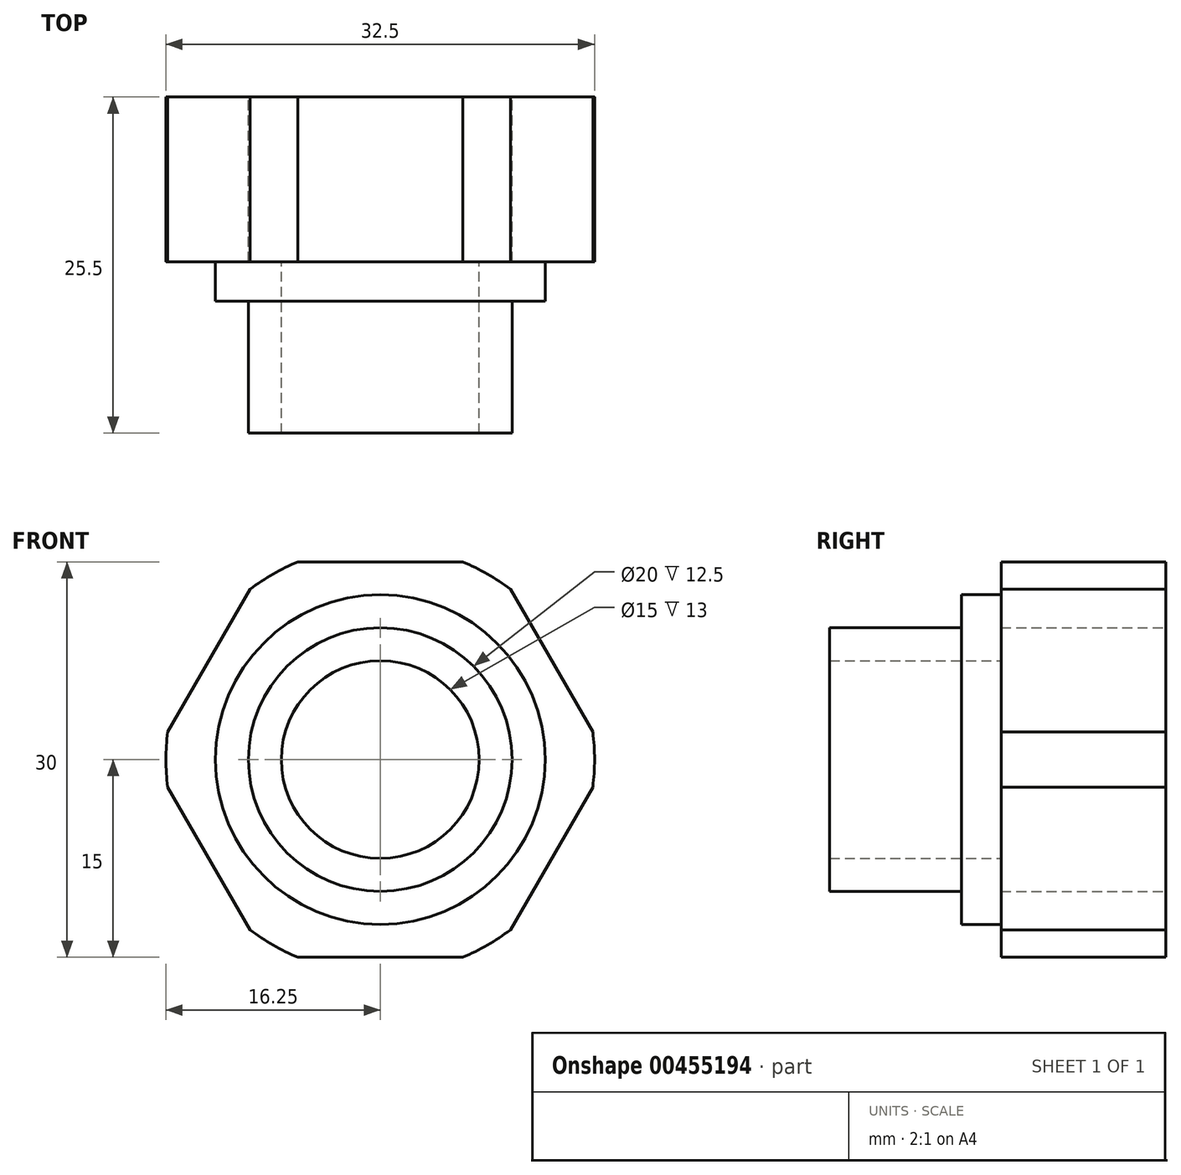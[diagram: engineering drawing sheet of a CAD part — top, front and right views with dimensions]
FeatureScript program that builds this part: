
annotation { "Feature Type Name" : "Feature", "Feature Type Description" : "" }
export const myFeature = defineFeature(function(context is Context, id is Id, definition is map)
    precondition{}
    {
        {
            var Q0;
            Q0=qCreatedBy(makeId("Front.planeOp"),FACE);
            var sketch = newSketch(context, id + "F0", { "sketchPlane" : qUnion([Q0])});
            skCircle(sketch, "E0.cCircle", {"center": v(0, 0) * mm, "radius": 15 * mm, "construction": true});
            skLineSegment(sketch, "E0.0", {"start": v(-8.66, 15) * mm, "end": v(8.66, 15) * mm});
            skLineSegment(sketch, "E0.1", {"start": v(8.66, 15) * mm, "end": v(17.32, 0) * mm});
            skLineSegment(sketch, "E0.2", {"start": v(17.32, 0) * mm, "end": v(8.66, -15) * mm});
            skLineSegment(sketch, "E0.3", {"start": v(8.66, -15) * mm, "end": v(-8.66, -15) * mm});
            skLineSegment(sketch, "E0.4", {"start": v(-8.66, -15) * mm, "end": v(-17.32, 0) * mm});
            skLineSegment(sketch, "E0.5", {"start": v(-17.32, 0) * mm, "end": v(-8.66, 15) * mm});
            skPoint(sketch, "E0.0.midPoint", {"position": v(0, 15) * mm});
            skCircle(sketch, "E1", {"center": v(0, 0) * mm, "radius": 10 * mm});
            skCircle(sketch, "E2", {"center": v(0, 0) * mm, "radius": 16.25 * mm});
            skSolve(sketch);
        }
        {
            var Q0;
            Q0=makeQuery(id+"F0.imprint","IMPRINT",FACE,{"disambiguationData":[TD([[makeQuery(id+"F0.imprint","IMPRINT",EDGE,{"derivedFrom":sQuery(id+"F0.wireOp",EDGE,"E1")}),-1.0]])]});
            extrude(context, id + "F1", {"entities" : qUnion([Q0]), "depth" : 12.5 * mm});
        }
        {
            var Q0;
            Q0=makeQuery(id+"F1.opExtrude","CAP_FACE",FACE,{"disambiguationData":[OSD([sQuery(id+"F0.wireOp",EDGE,"E0.0"),sQuery(id+"F0.wireOp",EDGE,"E0.1"),sQuery(id+"F0.wireOp",EDGE,"E0.2"),sQuery(id+"F0.wireOp",EDGE,"E0.3"),sQuery(id+"F0.wireOp",EDGE,"E0.4"),sQuery(id+"F0.wireOp",EDGE,"E0.5"),sQuery(id+"F0.wireOp",EDGE,"E1"),sQuery(id+"F0.wireOp",EDGE,"E2")])],"isStart":false});
            var sketch = newSketch(context, id + "F2", { "sketchPlane" : qUnion([Q0])});
            skCircle(sketch, "E3", {"center": v(0, 0) * mm, "radius": 12.5 * mm});
            skCircle(sketch, "E4", {"center": v(0, 0) * mm, "radius": 7.5 * mm});
            skSolve(sketch);
        }
        {
            var Q0;
            Q0 = qSketchRegion(id + "F2", true);
            extrude(context, id + "F3", {"entities" : qUnion([Q0]), "operationType" : NewBodyOperationType.ADD, "depth" : 3 * mm});
        }
        {
            var Q0;
            Q0=makeQuery(id+"F3.opExtrude","CAP_FACE",FACE,{"disambiguationData":[OSD([sQuery(id+"F2.wireOp",EDGE,"E3"),sQuery(id+"F2.wireOp",EDGE,"E4")])],"isStart":false});
            var sketch = newSketch(context, id + "F4", { "sketchPlane" : qUnion([Q0])});
            skCircle(sketch, "E5", {"center": v(0, 0) * mm, "radius": 10 * mm});
            skCircle(sketch, "E6", {"center": v(0, 0) * mm, "radius": 7.5 * mm});
            skSolve(sketch);
        }
        {
            var Q0;
            Q0 = qSketchRegion(id + "F4", true);
            extrude(context, id + "F5", {"entities" : qUnion([Q0]), "operationType" : NewBodyOperationType.ADD, "depth" : 10 * mm});
        }
    });
